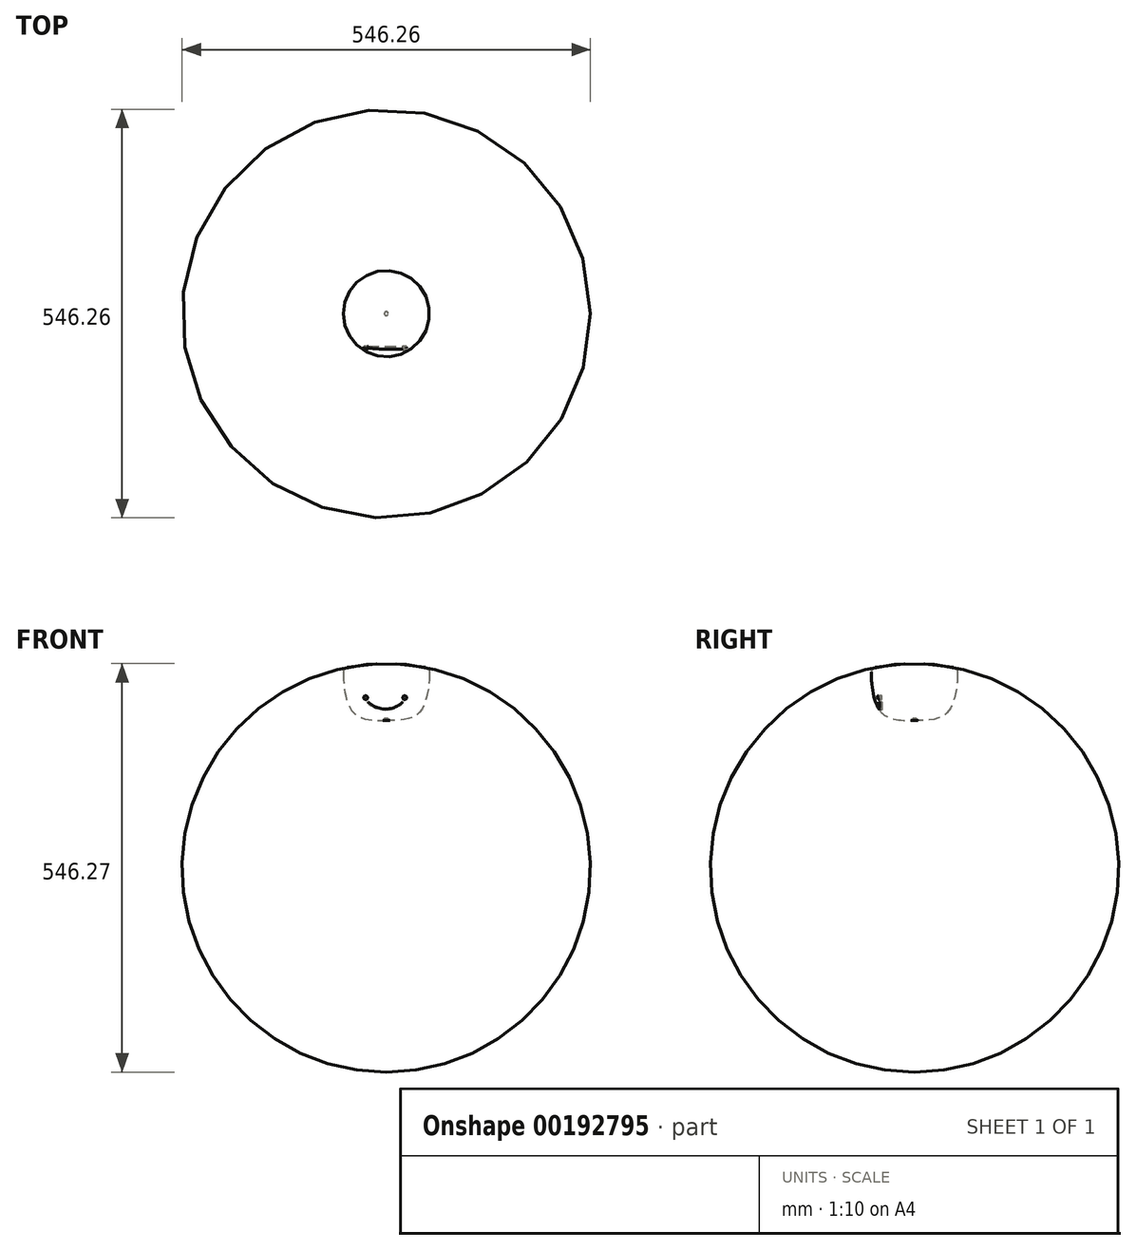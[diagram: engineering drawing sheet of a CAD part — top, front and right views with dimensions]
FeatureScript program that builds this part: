
annotation { "Feature Type Name" : "Feature", "Feature Type Description" : "" }
export const myFeature = defineFeature(function(context is Context, id is Id, definition is map)
    precondition{}
    {
        {
            var Q0;
            Q0=qCreatedBy(makeId("Front.planeOp"),FACE);
            var sketch = newSketch(context, id + "F0", { "sketchPlane" : qUnion([Q0])});
            skLineSegment(sketch, "E0", {"start": v(0, 0) * mm, "end": v(0, 50.8) * mm});
            skFitSpline(sketch, "E1", {"points": [v(38.1, 50.8) * mm, v(38.34, 38.11) * mm, v(35.07, 17.9) * mm, v(23.5, 3) * mm, v(0, 0) * mm], "startDerivative": vector(2.77, -59.25) * mm, "endDerivative": vector(-50.9, 0) * mm});
            skArc(sketch, "E2", {"start": v(34.9, 47.42) * mm, "mid": v(17.54, 49.95) * mm, "end": v(0, 50.8) * mm});
            skArc(sketch, "E3.filletArc", {"start": v(38.4, 43.26) * mm, "mid": v(37.4, 45.96) * mm, "end": v(34.9, 47.42) * mm});
            skLineSegment(sketch, "E4", {"start": v(0, 0) * mm, "end": v(3.18, 0) * mm});
            skSolve(sketch);
        }
        {
            var Q0;
            Q0=qSketchRegion(id+"F0",true);
            var Q1;
            Q1=sQuery(id+"F0.wireOp",EDGE,"E0");
            revolve(context, id + "F1", {"entities" : qUnion([Q0]), "axis" : qUnion([Q1]), "revolveType" : RevolveType.FULL});
        }
        {
            var Q0;
            Q0=qCreatedBy(makeId("Front.planeOp"),FACE);
            cPlane(context, id + "F2", {"entities" : qUnion([Q0]), "cplaneType" : CPlaneType.OFFSET, "offset" : 50.8 * mm, "width" : 152.4 * mm, "height" : 152.4 * mm});
        }
        {
            var Q0;
            Q0=qCreatedBy(id+"F2.planeOp",FACE);
            var sketch = newSketch(context, id + "F3", { "sketchPlane" : qUnion([Q0])});
            skCircle(sketch, "E5", {"center": v(-18.39, 20.46) * mm, "radius": 1.71 * mm});
            skCircle(sketch, "E6", {"center": v(16.34, 20.46) * mm, "radius": 1.71 * mm});
            skArc(sketch, "E7", {"start": v(-16.37, 16.82) * mm, "mid": v(-0.97, 10.33) * mm, "end": v(14.54, 16.58) * mm});
            skArc(sketch, "E8.0", {"start": v(-16.9, 16.3) * mm, "mid": v(-0.97, 9.58) * mm, "end": v(15.06, 16.05) * mm});
            skLineSegment(sketch, "E9", {"start": v(-16.37, 16.82) * mm, "end": v(-16.9, 16.3) * mm});
            skLineSegment(sketch, "E10", {"start": v(14.54, 16.58) * mm, "end": v(15.06, 16.05) * mm});
            skSolve(sketch);
        }
        {
            var Q0;
            Q0=qSketchRegion(id+"F3",true);
            extrude(context, id + "F4", {"entities" : qUnion([Q0]), "oppositeDirection" : true, "depth" : 21.59 * mm});
        }
        {
            var Q0;
            Q0=makeQuery(id+"F4.opExtrude","SWEPT_BODY",BODY,{"disambiguationData":[OSD([sQuery(id+"F3.wireOp",EDGE,"E5")])]});
            var Q1;
            Q1=makeQuery(id+"F4.opExtrude","SWEPT_BODY",BODY,{"disambiguationData":[OSD([sQuery(id+"F3.wireOp",EDGE,"E7"),sQuery(id+"F3.wireOp",EDGE,"E8.0"),sQuery(id+"F3.wireOp",EDGE,"E9"),sQuery(id+"F3.wireOp",EDGE,"E10")])]});
            var Q2;
            Q2=makeQuery(id+"F4.opExtrude","SWEPT_BODY",BODY,{"disambiguationData":[OSD([sQuery(id+"F3.wireOp",EDGE,"E6")])]});
            var Q3;
            Q3=makeQuery(id+"F1.opRevolve","SWEPT_BODY",BODY,{"disambiguationData":[OSD([sQuery(id+"F0.wireOp",EDGE,"E0"),sQuery(id+"F0.wireOp",EDGE,"2ab0945a-3d79-4475-b4e3-0925875c39e2"),sQuery(id+"F0.wireOp",EDGE,"52c6e8fe-6c53-4660-81ae-a93639e3b140")])]});
            booleanBodies(context, id + "F5", {"operationType" : BooleanOperationType.SUBTRACTION, "tools" : qUnion([Q0, Q1, Q2]), "targets" : qUnion([Q3])});
        }
        {
            var Q0;
            Q0=makeQuery(id+"F1.opRevolve","SWEPT_BODY",BODY,{"disambiguationData":[OSD([sQuery(id+"F0.wireOp",EDGE,"E0"),sQuery(id+"F0.wireOp",EDGE,"2ab0945a-3d79-4475-b4e3-0925875c39e2"),sQuery(id+"F0.wireOp",EDGE,"52c6e8fe-6c53-4660-81ae-a93639e3b140")])]});
            var Q1;
            Q1=qCreatedBy(makeId("Origin.pointOp"),VERTEX);
            transform(context, id + "F6", {"entities" : qUnion([Q0]), "transformType" : TransformType.SCALE_UNIFORMLY, "scale" : 1.5, "makeCopy" : false, "scalePoint" : qUnion([Q1])});
        }
        {
            var Q0;
            Q0=qCreatedBy(makeId("Top.planeOp"),FACE);
            var sketch = newSketch(context, id + "F7", { "sketchPlane" : qUnion([Q0])});
            skCircle(sketch, "E11", {"center": v(0, 0) * mm, "radius": 2.57 * mm});
            skSolve(sketch);
        }
        {
            var Q0;
            Q0=qSketchRegion(id+"F7",true);
            extrude(context, id + "F8", {"entities" : qUnion([Q0]), "operationType" : NewBodyOperationType.REMOVE, "depth" : 2.54 * mm});
        }
    });
